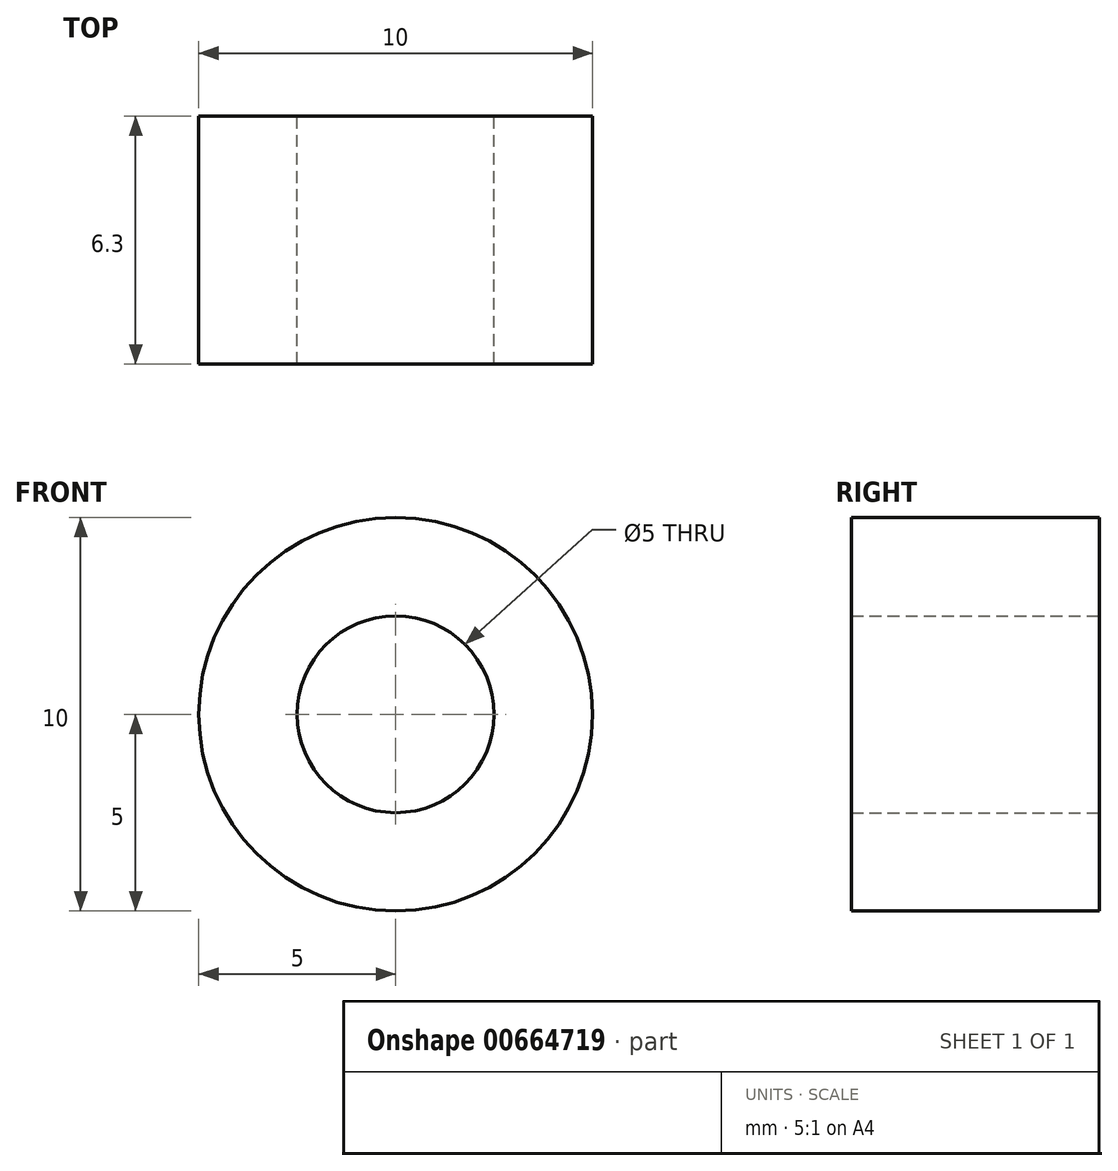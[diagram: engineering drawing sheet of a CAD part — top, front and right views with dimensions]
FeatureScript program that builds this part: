
annotation { "Feature Type Name" : "Feature", "Feature Type Description" : "" }
export const myFeature = defineFeature(function(context is Context, id is Id, definition is map)
    precondition{}
    {
        {
            var Q0;
            Q0=qCreatedBy(makeId("Front.planeOp"),FACE);
            var sketch = newSketch(context, id + "F0", { "sketchPlane" : qUnion([Q0])});
            skCircle(sketch, "E0", {"center": v(0, 0) * mm, "radius": 2.5 * mm});
            skCircle(sketch, "E1", {"center": v(0, 0) * mm, "radius": 5 * mm});
            skSolve(sketch);
        }
        {
            var Q0;
            Q0=makeQuery(id+"F0.imprint","IMPRINT",FACE,{"disambiguationData":[TD([[makeQuery(id+"F0.imprint","IMPRINT",EDGE,{"derivedFrom":sQuery(id+"F0.wireOp",EDGE,"E0")}),-1.0]])]});
            extrude(context, id + "F1", {"entities" : qUnion([Q0]), "depth" : 6.3 * mm, "offsetDistance" : 25 * mm});
        }
    });
